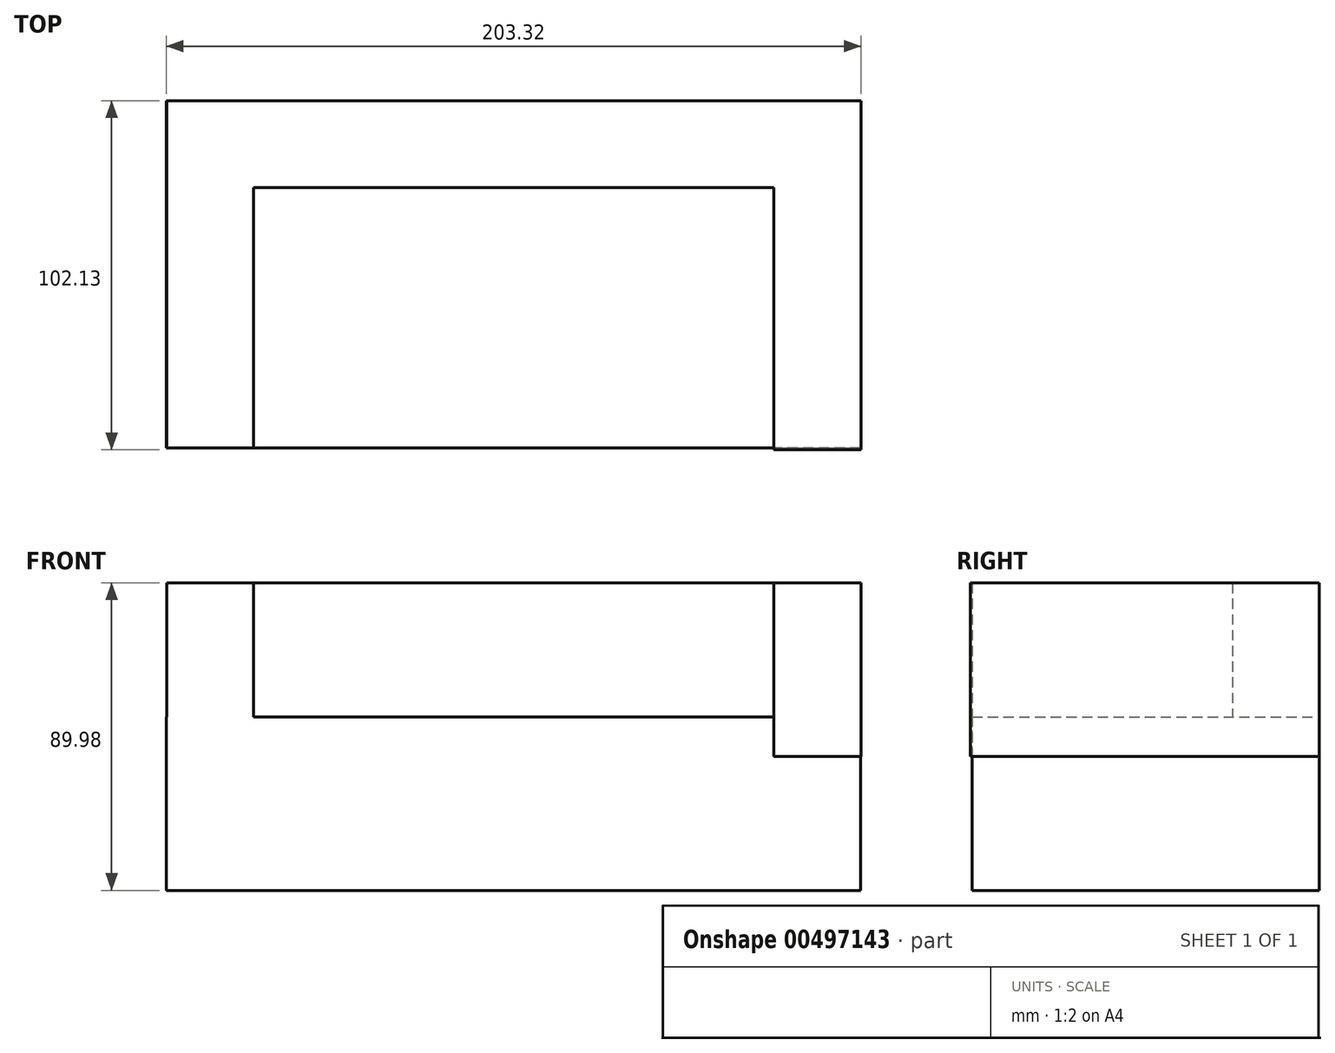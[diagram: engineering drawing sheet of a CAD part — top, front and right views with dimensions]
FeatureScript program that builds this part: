
annotation { "Feature Type Name" : "Feature", "Feature Type Description" : "" }
export const myFeature = defineFeature(function(context is Context, id is Id, definition is map)
    precondition{}
    {
        {
            var Q0;
            Q0=qCreatedBy(makeId("Front.planeOp"),FACE);
            var sketch = newSketch(context, id + "F0", { "sketchPlane" : qUnion([Q0])});
            skLineSegment(sketch, "E0.bottom", {"start": v(-52.6, 11.62) * mm, "end": v(150.6, 11.62) * mm});
            skLineSegment(sketch, "E0.top", {"start": v(-52.6, -39.18) * mm, "end": v(150.6, -39.18) * mm});
            skLineSegment(sketch, "E0.left", {"start": v(-52.6, 11.62) * mm, "end": v(-52.6, -39.18) * mm});
            skLineSegment(sketch, "E0.right", {"start": v(150.6, 11.62) * mm, "end": v(150.6, -39.18) * mm});
            skSolve(sketch);
        }
        {
            var Q0;
            Q0 = qSketchRegion(id + "F0", true);
            extrude(context, id + "F1", {"entities" : qUnion([Q0]), "depth" : 101.6 * mm, "offsetDistance" : 25.4 * mm});
        }
        {
            var Q0;
            Q0=qCreatedBy(makeId("Top.planeOp"),FACE);
            var sketch = newSketch(context, id + "F2", { "sketchPlane" : qUnion([Q0])});
            skLineSegment(sketch, "E1.bottom", {"start": v(-52.47, 0) * mm, "end": v(-27.07, 0) * mm});
            skLineSegment(sketch, "E1.top", {"start": v(-52.47, -101.6) * mm, "end": v(-27.07, -101.6) * mm});
            skLineSegment(sketch, "E1.left", {"start": v(-52.47, 0) * mm, "end": v(-52.47, -101.6) * mm});
            skLineSegment(sketch, "E1.right", {"start": v(-27.07, 0) * mm, "end": v(-27.07, -101.6) * mm});
            skLineSegment(sketch, "E2.bottom", {"start": v(-52.47, 0) * mm, "end": v(150.73, 0) * mm});
            skLineSegment(sketch, "E2.top", {"start": v(-52.47, -25.37) * mm, "end": v(150.73, -25.37) * mm});
            skLineSegment(sketch, "E2.left", {"start": v(-52.47, 0) * mm, "end": v(-52.47, -25.37) * mm});
            skLineSegment(sketch, "E2.right", {"start": v(150.73, 0) * mm, "end": v(150.73, -25.37) * mm});
            skLineSegment(sketch, "E3.bottom", {"start": v(150.73, 0) * mm, "end": v(125.51, 0) * mm});
            skLineSegment(sketch, "E3.top", {"start": v(150.73, -25.4) * mm, "end": v(125.51, -25.4) * mm});
            skLineSegment(sketch, "E3.left", {"start": v(150.73, 0) * mm, "end": v(150.73, -25.4) * mm});
            skLineSegment(sketch, "E3.right", {"start": v(125.51, 0) * mm, "end": v(125.51, -25.4) * mm});
            skLineSegment(sketch, "E4.bottom", {"start": v(150.73, 0) * mm, "end": v(125.26, 0) * mm});
            skLineSegment(sketch, "E4.top", {"start": v(150.73, -102.13) * mm, "end": v(125.26, -102.13) * mm});
            skLineSegment(sketch, "E4.left", {"start": v(150.73, 0) * mm, "end": v(150.73, -102.13) * mm});
            skLineSegment(sketch, "E4.right", {"start": v(125.26, 0) * mm, "end": v(125.26, -102.13) * mm});
            skSolve(sketch);
        }
        {
            var Q0;
            Q0 = qSketchRegion(id + "F2", true);
            extrude(context, id + "F3", {"entities" : qUnion([Q0]), "operationType" : NewBodyOperationType.ADD, "depth" : 50.8 * mm, "offsetDistance" : 25.4 * mm});
        }
    });
